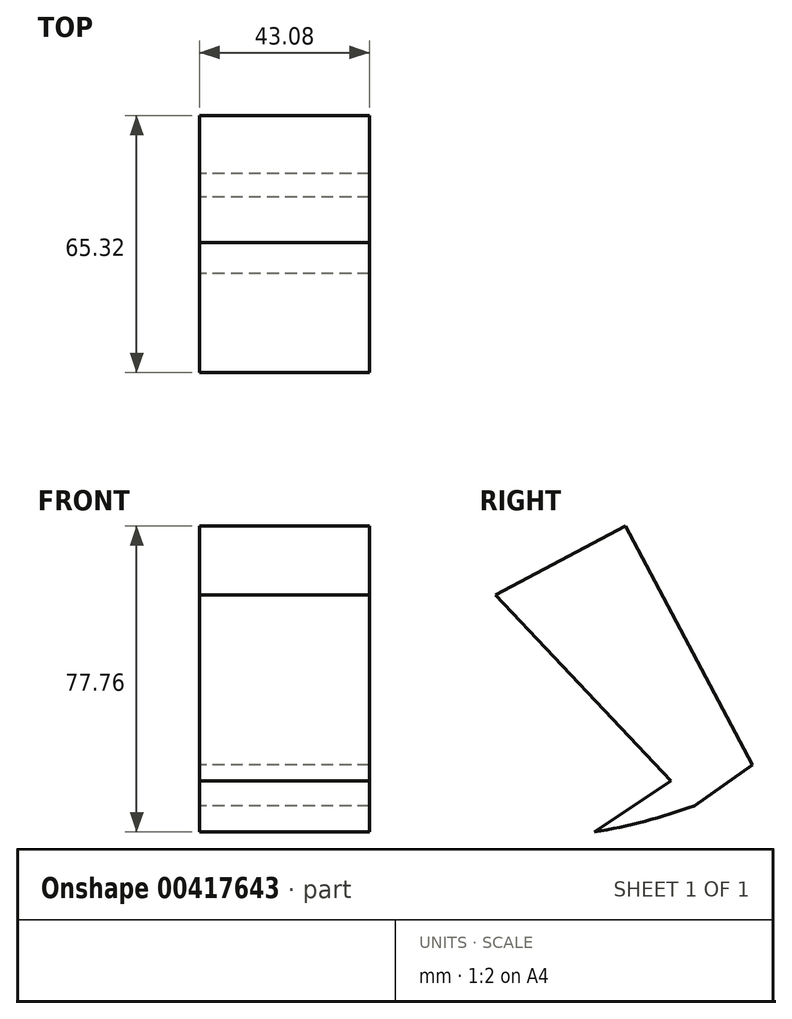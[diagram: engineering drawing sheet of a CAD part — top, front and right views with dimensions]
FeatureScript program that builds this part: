
annotation { "Feature Type Name" : "Feature", "Feature Type Description" : "" }
export const myFeature = defineFeature(function(context is Context, id is Id, definition is map)
    precondition{}
    {
        {
            var Q0;
            Q0=qCreatedBy(makeId("Right.planeOp"),FACE);
            var sketch = newSketch(context, id + "F0", { "sketchPlane" : qUnion([Q0])});
            skLineSegment(sketch, "E0", {"start": v(25.37, -34.27) * mm, "end": v(-25.17, 19.24) * mm});
            skArc(sketch, "E1", {"start": v(0, -40.96) * mm, "mid": v(12.84, -38.2) * mm, "end": v(25.37, -34.27) * mm});
            skLineSegment(sketch, "E2", {"start": v(-25.17, 19.24) * mm, "end": v(7.9, 36.8) * mm});
            skLineSegment(sketch, "E3", {"start": v(7.9, 36.8) * mm, "end": v(40.15, -23.93) * mm});
            skLineSegment(sketch, "E4", {"start": v(40.15, -23.93) * mm, "end": v(25.37, -23.93) * mm});
            skLineSegment(sketch, "E5", {"start": v(25.37, -23.93) * mm, "end": v(0, -40.96) * mm});
            skLineSegment(sketch, "E6", {"start": v(40.15, -23.93) * mm, "end": v(25.37, -34.27) * mm});
            skSolve(sketch);
        }
        {
            var Q0;
            Q0 = qSketchRegion(id + "F0", true);
            var Q1;
            {var subQ4=sQuery(id+"F0.wireOp",EDGE,"E4");Q1=makeQuery(id+"F0.imprint","IMPRINT",FACE,{"disambiguationData":[TD([[makeQuery(id+"F0.imprint","IMPRINT",EDGE,{"derivedFrom":subQ4}),1.0]])]});}
            var Q2;
            {var subQ1=sQuery(id+"F0.wireOp",EDGE,"E2");Q2=makeQuery(id+"F0.imprint","IMPRINT",FACE,{"disambiguationData":[TD([[makeQuery(id+"F0.imprint","IMPRINT",EDGE,{"derivedFrom":subQ1}),-1.0]])]});}
            var Q3;
            {var subQ0=sQuery(id+"F0.wireOp",EDGE,"E1");Q3=makeQuery(id+"F0.imprint","IMPRINT",FACE,{"disambiguationData":[TD([[makeQuery(id+"F0.imprint","IMPRINT",EDGE,{"derivedFrom":subQ0}),1.0]])]});}
            extrude(context, id + "F1", {"entities" : qUnion([Q0, Q1, Q2, Q3]), "depth" : 43.08 * mm});
        }
    });
